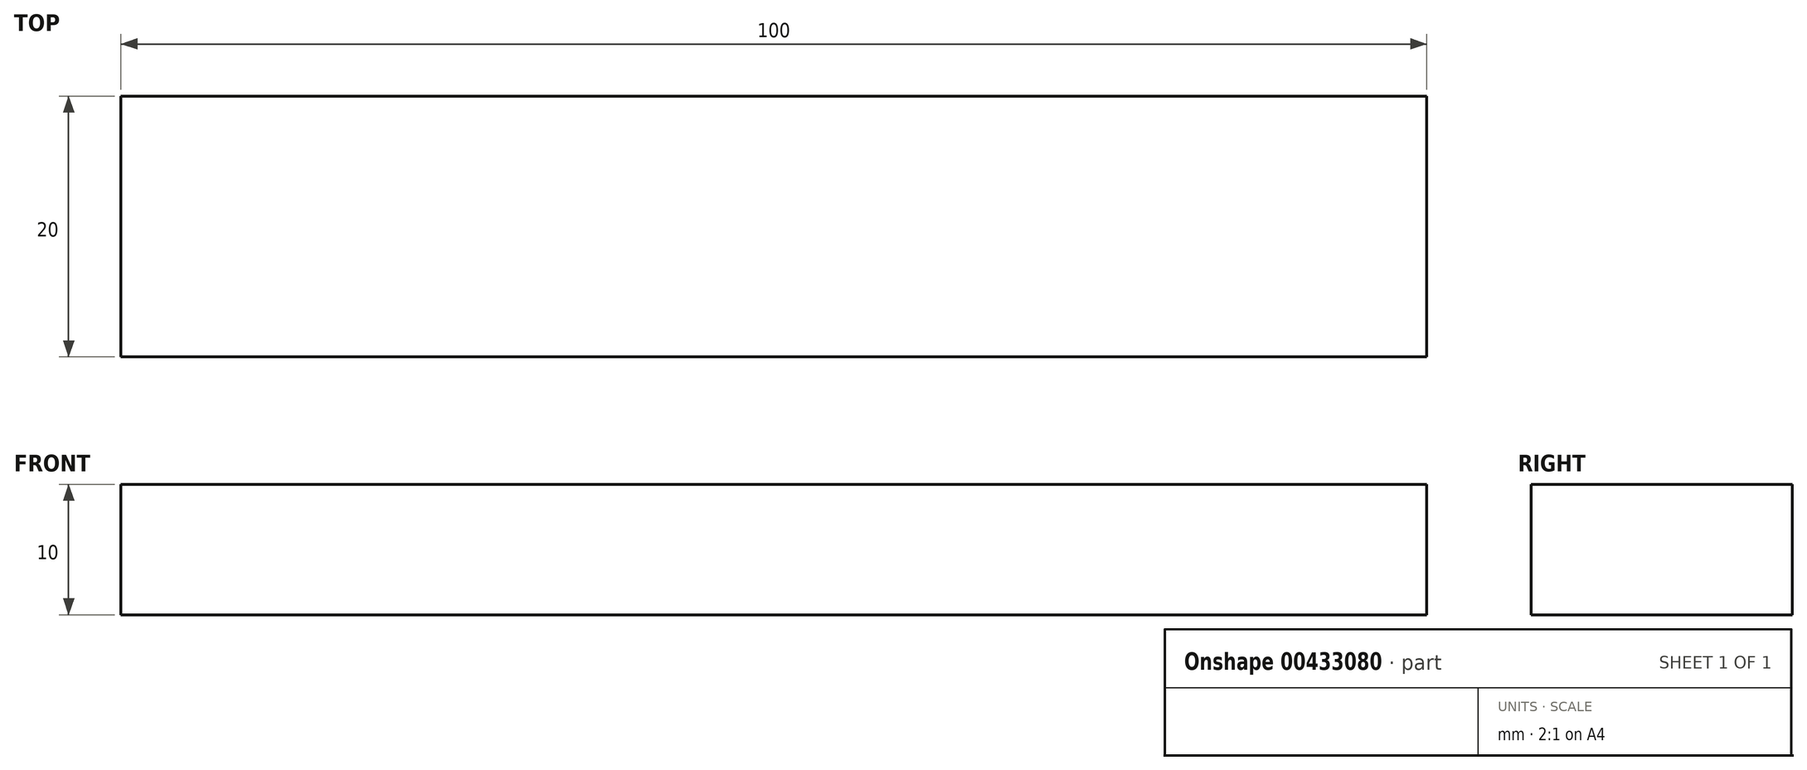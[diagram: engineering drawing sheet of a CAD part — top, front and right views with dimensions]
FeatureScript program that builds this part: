
annotation { "Feature Type Name" : "Feature", "Feature Type Description" : "" }
export const myFeature = defineFeature(function(context is Context, id is Id, definition is map)
    precondition{}
    {
        {
            var Q0;
            Q0=qCreatedBy(makeId("Top.planeOp"),FACE);
            var sketch = newSketch(context, id + "F0", { "sketchPlane" : qUnion([Q0])});
            skLineSegment(sketch, "E0.bottom", {"start": v(-49.1, 37.55) * mm, "end": v(50.9, 37.55) * mm});
            skLineSegment(sketch, "E0.top", {"start": v(-49.1, 17.55) * mm, "end": v(50.9, 17.55) * mm});
            skLineSegment(sketch, "E0.left", {"start": v(-49.1, 37.55) * mm, "end": v(-49.1, 17.55) * mm});
            skLineSegment(sketch, "E0.right", {"start": v(50.9, 37.55) * mm, "end": v(50.9, 17.55) * mm});
            skLineSegment(sketch, "E1.bottom", {"start": v(-49.1, 17.55) * mm, "end": v(-29.1, 17.55) * mm});
            skLineSegment(sketch, "E1.top", {"start": v(-49.1, -57.45) * mm, "end": v(-29.1, -57.45) * mm});
            skLineSegment(sketch, "E1.left", {"start": v(-49.1, 17.55) * mm, "end": v(-49.1, -57.45) * mm});
            skLineSegment(sketch, "E1.right", {"start": v(-29.1, 17.55) * mm, "end": v(-29.1, -57.45) * mm});
            skLineSegment(sketch, "E2.bottom", {"start": v(50.9, 17.55) * mm, "end": v(30.9, 17.55) * mm});
            skLineSegment(sketch, "E2.top", {"start": v(50.9, -57.45) * mm, "end": v(30.9, -57.45) * mm});
            skLineSegment(sketch, "E2.left", {"start": v(50.9, 17.55) * mm, "end": v(50.9, -57.45) * mm});
            skLineSegment(sketch, "E2.right", {"start": v(30.9, 17.55) * mm, "end": v(30.9, -57.45) * mm});
            skSolve(sketch);
        }
        {
            var Q0;
            Q0=makeQuery(id+"F0.imprint","IMPRINT",FACE,{"disambiguationData":[TD([[makeQuery(id+"F0.imprint","IMPRINT",EDGE,{"derivedFrom":sQuery(id+"F0.wireOp",EDGE,"E0.bottom")}),-1.0]])]});
            var Q1;
            Q1=makeQuery(id+"F0.imprint","IMPRINT",FACE,{"disambiguationData":[TD([[makeQuery(id+"F0.imprint","IMPRINT",EDGE,{"derivedFrom":sQuery(id+"F0.wireOp",EDGE,"E1.bottom")}),-1.0]])]});
            var Q2;
            Q2=makeQuery(id+"F0.imprint","IMPRINT",FACE,{"disambiguationData":[TD([[makeQuery(id+"F0.imprint","IMPRINT",EDGE,{"derivedFrom":sQuery(id+"F0.wireOp",EDGE,"E2.bottom")}),1.0]])]});
            extrude(context, id + "F1", {"entities" : qUnion([Q0, Q1, Q2]), "depth" : 10 * mm});
        }
    });
